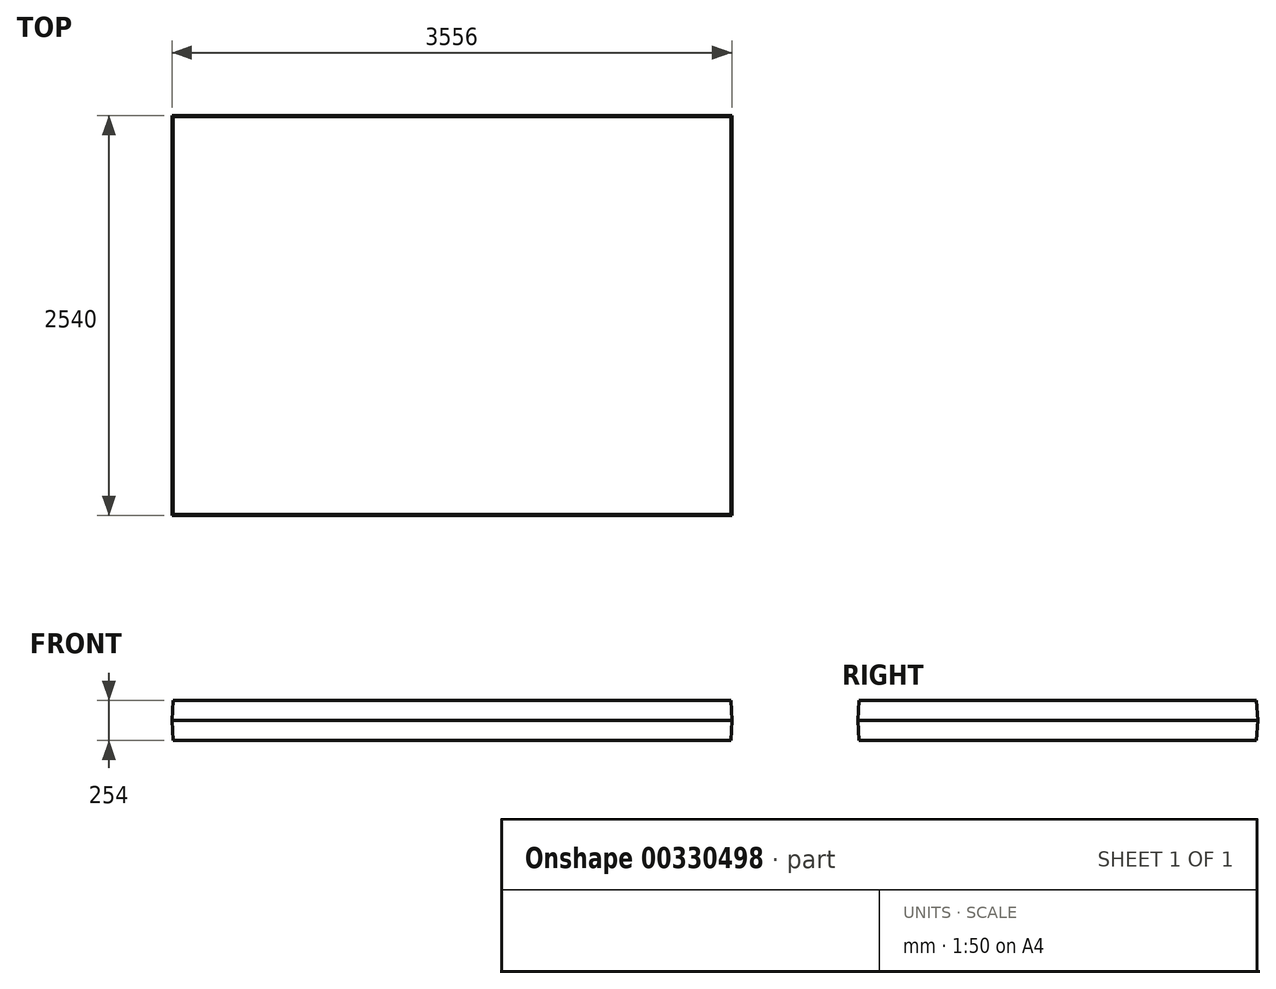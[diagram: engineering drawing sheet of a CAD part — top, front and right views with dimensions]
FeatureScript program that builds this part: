
annotation { "Feature Type Name" : "Feature", "Feature Type Description" : "" }
export const myFeature = defineFeature(function(context is Context, id is Id, definition is map)
    precondition{}
    {
        {
            var Q0;
            Q0=qCreatedBy(makeId("Top.planeOp"),FACE);
            var sketch = newSketch(context, id + "F0", { "sketchPlane" : qUnion([Q0])});
            skLineSegment(sketch, "E0", {"start": v(0, 0.1) * mm, "end": v(3556, 0.1) * mm});
            skLineSegment(sketch, "E1", {"start": v(3556, 0.1) * mm, "end": v(3556, -2539.9) * mm});
            skLineSegment(sketch, "E2", {"start": v(3556, -2539.9) * mm, "end": v(0, -2539.9) * mm});
            skLineSegment(sketch, "E3", {"start": v(0, -2539.9) * mm, "end": v(0, 0.1) * mm});
            skSolve(sketch);
        }
        {
            var Q0;
            Q0=makeQuery(id+"F0.imprint","IMPRINT",FACE,{"disambiguationData":[TD([[makeQuery(id+"F0.imprint","IMPRINT",EDGE,{"derivedFrom":sQuery(id+"F0.wireOp",EDGE,"E0")}),-1.0]])]});
            extrude(context, id + "F1", {"entities" : qUnion([Q0]), "endBound" : BoundingType.SYMMETRIC, "depth" : 254 * mm, "hasDraft" : true, "draftAngle" : 3 * degree, "draftPullDirection" : true});
        }
    });
